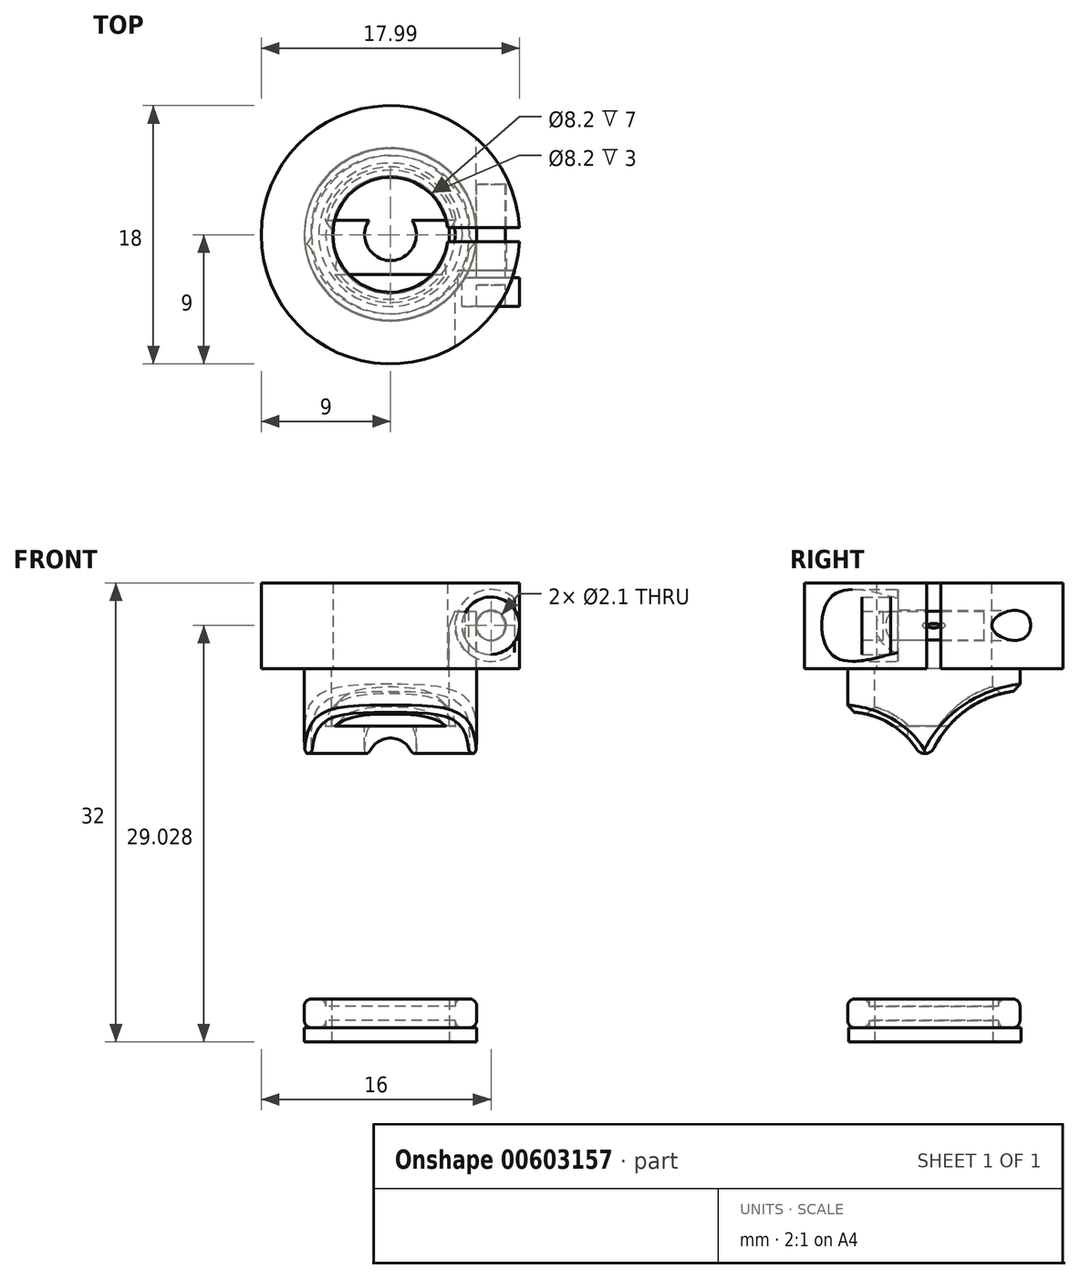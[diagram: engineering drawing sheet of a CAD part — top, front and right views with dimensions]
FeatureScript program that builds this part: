
annotation { "Feature Type Name" : "Feature", "Feature Type Description" : "" }
export const myFeature = defineFeature(function(context is Context, id is Id, definition is map)
    precondition{}
    {
        {
            var Q0;
            Q0=qCreatedBy(makeId("Top.planeOp"),FACE);
            var sketch = newSketch(context, id + "F0", { "sketchPlane" : qUnion([Q0])});
            skCircle(sketch, "E0", {"center": v(0, 0) * mm, "radius": 6 * mm});
            skCircle(sketch, "E1", {"center": v(0, 0) * mm, "radius": 4.5 * mm});
            skSolve(sketch);
        }
        {
            var Q0;
            Q0=makeQuery(id+"F0.imprint","IMPRINT",FACE,{"disambiguationData":[TD([[makeQuery(id+"F0.imprint","IMPRINT",EDGE,{"derivedFrom":sQuery(id+"F0.wireOp",EDGE,"E0")}),1.0]])]});
            extrude(context, id + "F1", {"entities" : qUnion([Q0]), "depth" : 2 * mm, "offsetDistance" : 25 * mm});
        }
        {
            var Q0;
            Q0=makeQuery(id+"F1.opExtrude","CAP_EDGE",EDGE,{"disambiguationData":[OSD([sQuery(id+"F0.wireOp",EDGE,"E0")])],"isStart":false});
            var Q1;
            Q1=makeQuery(id+"F1.opExtrude","CAP_EDGE",EDGE,{"disambiguationData":[OSD([sQuery(id+"F0.wireOp",EDGE,"E1")])],"isStart":false});
            var Q2;
            Q2=makeQuery(id+"F1.opExtrude","CAP_EDGE",EDGE,{"disambiguationData":[OSD([sQuery(id+"F0.wireOp",EDGE,"E0")])],"isStart":true});
            var Q3;
            Q3=makeQuery(id+"F1.opExtrude","CAP_EDGE",EDGE,{"disambiguationData":[OSD([sQuery(id+"F0.wireOp",EDGE,"E1")])],"isStart":true});
            fillet(context, id + "F2", {"entities" : qUnion([Q0, Q1, Q2, Q3]), "radius" : .5 * mm, "tangentPropagation" : true, "allowEdgeOverflow" : false});
        }
        {
            var Q0;
            Q0=qCreatedBy(makeId("Top.planeOp"),FACE);
            var sketch = newSketch(context, id + "F3", { "sketchPlane" : qUnion([Q0])});
            skCircle(sketch, "E2", {"center": v(0, 0) * mm, "radius": 4.1 * mm});
            skCircle(sketch, "E3", {"center": v(0, 0.06) * mm, "radius": 6 * mm});
            skCircle(sketch, "E4", {"center": v(0, 0) * mm, "radius": 4.5 * mm});
            skSolve(sketch);
        }
        {
            var Q0;
            Q0=makeQuery(id+"F3.imprint","IMPRINT",FACE,{"disambiguationData":[TD([[makeQuery(id+"F3.imprint","IMPRINT",EDGE,{"derivedFrom":sQuery(id+"F3.wireOp",EDGE,"E2")}),-1.0]])]});
            extrude(context, id + "F4", {"entities" : qUnion([Q0]), "depth" : 2 * mm, "offsetDistance" : 25 * mm});
        }
        {
            var Q0;
            Q0=makeQuery(id+"F3.imprint","IMPRINT",FACE,{"disambiguationData":[TD([[makeQuery(id+"F3.imprint","IMPRINT",EDGE,{"derivedFrom":sQuery(id+"F3.wireOp",EDGE,"E2")}),-1.0]])]});
            var Q1;
            Q1=makeQuery(id+"F3.imprint","IMPRINT",FACE,{"disambiguationData":[TD([[makeQuery(id+"F3.imprint","IMPRINT",EDGE,{"derivedFrom":sQuery(id+"F3.wireOp",EDGE,"E3")}),1.0]])]});
            extrude(context, id + "F5", {"entities" : qUnion([Q0, Q1]), "operationType" : NewBodyOperationType.ADD, "oppositeDirection" : true, "depth" : 1 * mm, "offsetDistance" : 25 * mm});
        }
        {
            var Q0;
            Q0=qCreatedBy(makeId("Top.planeOp"),FACE);
            cPlane(context, id + "F6", {"entities" : qUnion([Q0]), "cplaneType" : CPlaneType.OFFSET, "offset" : 25 * mm, "width" : 150 * mm, "height" : 150 * mm});
        }
        {
            var Q0;
            Q0=qCreatedBy(id+"F6.planeOp",FACE);
            var sketch = newSketch(context, id + "F7", { "sketchPlane" : qUnion([Q0])});
            skCircle(sketch, "E5", {"center": v(0, 0) * mm, "radius": 4 * mm});
            skCircle(sketch, "E6", {"center": v(0, 0) * mm, "radius": 9 * mm});
            skLineSegment(sketch, "E7", {"start": v(3.97, 0.5) * mm, "end": v(8.99, 0.5) * mm});
            skLineSegment(sketch, "E8.MirrorCS", {"start": v(3.97, -0.5) * mm, "end": v(8.99, -0.5) * mm});
            skSolve(sketch);
        }
        {
            var Q0;
            {var subQ0=sQuery(id+"F7.wireOp",EDGE,"E7");Q0=makeQuery(id+"F7.imprint","IMPRINT",FACE,{"disambiguationData":[TD([[makeQuery(id+"F7.imprint","IMPRINT",EDGE,{"derivedFrom":subQ0}),1.0]])]});}
            extrude(context, id + "F8", {"entities" : qUnion([Q0]), "depth" : 6 * mm, "offsetDistance" : 25 * mm});
        }
        {
            var Q0;
            Q0=qCreatedBy(makeId("Front.planeOp"),FACE);
            var sketch = newSketch(context, id + "F9", { "sketchPlane" : qUnion([Q0])});
            skCircle(sketch, "E9", {"center": v(7, 28.03) * mm, "radius": 2.5 * mm});
            skSolve(sketch);
        }
        {
            var Q0;
            Q0=sQuery(id+"F9.wireOp",VERTEX,"E9.center");
            var Q1;
            Q1=makeQuery(id+"F8.opExtrude","SWEPT_BODY",BODY,{"disambiguationData":[OSD([sQuery(id+"F7.wireOp",EDGE,"E5"),sQuery(id+"F7.wireOp",EDGE,"E6"),sQuery(id+"F7.wireOp",EDGE,"E7"),sQuery(id+"F7.wireOp",EDGE,"E8.MirrorCS")])]});
            hole(context, id + "F10", {"style" : HoleStyle.SIMPLE, "endStyle" : HoleEndStyle.THROUGH, "holeDiameter" : 2.1 * mm, "majorDiameter" : 5 * mm, "isTappedThrough" : true, "tappedDepth" : 6 * mm, "tapClearance" : 3, "startFromSketch" : true, "locations" : qUnion([Q0]), "scope" : qUnion([Q1])});
        }
        {
            var Q0;
            Q0=sQuery(id+"F9.wireOp",VERTEX,"E9.center");
            var Q1;
            Q1=makeQuery(id+"F8.opExtrude","SWEPT_BODY",BODY,{"disambiguationData":[OSD([sQuery(id+"F7.wireOp",EDGE,"E5"),sQuery(id+"F7.wireOp",EDGE,"E6"),sQuery(id+"F7.wireOp",EDGE,"E7"),sQuery(id+"F7.wireOp",EDGE,"E8.MirrorCS")])]});
            hole(context, id + "F11", {"style" : HoleStyle.SIMPLE, "endStyle" : HoleEndStyle.THROUGH, "oppositeDirection" : true, "holeDiameter" : 2.1 * mm, "majorDiameter" : 5 * mm, "isTappedThrough" : true, "tappedDepth" : 6 * mm, "tapClearance" : 3, "startFromSketch" : true, "locations" : qUnion([Q0]), "scope" : qUnion([Q1])});
        }
        {
            var Q0;
            Q0=makeQuery(id+"F9.imprint","IMPRINT",FACE,{"disambiguationData":[TD([[makeQuery(id+"F9.imprint","IMPRINT",EDGE,{"derivedFrom":sQuery(id+"F9.wireOp",EDGE,"E9")}),1.0]])]});
            var Q1;
            Q1=sQuery(id+"F9.wireOp",EDGE,"E9");
            extrude(context, id + "F12", {"entities" : qUnion([Q0]), "operationType" : NewBodyOperationType.REMOVE, "surfaceEntities" : qUnion([Q1]), "depth" : 10 * mm, "offsetDistance" : 25 * mm, "hasSecondDirection" : true, "secondDirectionOppositeDirection" : false, "secondDirectionDepth" : 2.5 * mm});
        }
        {
            var Q0;
            Q0=qCreatedBy(makeId("Front.planeOp"),FACE);
            var sketch = newSketch(context, id + "F13", { "sketchPlane" : qUnion([Q0])});
            skCircle(sketch, "E10", {"center": v(6.99, 28) * mm, "radius": 2 * mm});
            skCircle(sketch, "E11", {"center": v(6.99, 28) * mm, "radius": 1 * mm});
            skSolve(sketch);
        }
        {
            var Q0;
            Q0=makeQuery(id+"F13.imprint","IMPRINT",FACE,{"disambiguationData":[TD([[makeQuery(id+"F13.imprint","IMPRINT",EDGE,{"derivedFrom":sQuery(id+"F13.wireOp",EDGE,"E11")}),1.0]])]});
            extrude(context, id + "F14", {"entities" : qUnion([Q0]), "depth" : 7 * mm, "offsetDistance" : 25 * mm, "symmetric" : true});
        }
        {
            var Q0;
            Q0=makeQuery(id+"F13.imprint","IMPRINT",FACE,{"disambiguationData":[TD([[makeQuery(id+"F13.imprint","IMPRINT",EDGE,{"derivedFrom":sQuery(id+"F13.wireOp",EDGE,"E10")}),1.0]])]});
            extrude(context, id + "F15", {"entities" : qUnion([Q0]), "operationType" : NewBodyOperationType.ADD, "depth" : 5 * mm, "offsetDistance" : 25 * mm, "hasSecondDirection" : true, "secondDirectionOppositeDirection" : false, "secondDirectionDepth" : 3 * mm});
        }
        {
            var Q0;
            Q0=makeQuery(id+"F8.opExtrude","CAP_FACE",FACE,{"disambiguationData":[OSD([sQuery(id+"F7.wireOp",EDGE,"E5"),sQuery(id+"F7.wireOp",EDGE,"E6"),sQuery(id+"F7.wireOp",EDGE,"E7"),sQuery(id+"F7.wireOp",EDGE,"E8.MirrorCS")])],"isStart":true});
            var sketch = newSketch(context, id + "F16", { "sketchPlane" : qUnion([Q0])});
            skCircle(sketch, "E12", {"center": v(0, 0) * mm, "radius": 4.1 * mm});
            skCircle(sketch, "E13", {"center": v(0, 0) * mm, "radius": 6 * mm});
            skSolve(sketch);
        }
        {
            var Q0;
            {var subQ0=sQuery(id+"F16.wireOp",EDGE,"E12");var subQ1=makeQuery(id+"F8.opExtrude","CAP_EDGE",EDGE,{"disambiguationData":[OSD([sQuery(id+"F7.wireOp",EDGE,"E7")])],"isStart":true});var subQ2=makeQuery(id+"F16.imprint","INTERSECT",VERTEX,{"derivedFrom":[subQ1,subQ0]});Q0=makeQuery(id+"F16.imprint","IMPRINT",FACE,{"disambiguationData":[TD([[makeQuery(id+"F16.imprint","IMPRINT",EDGE,{"disambiguationData":[TD([[subQ2,1.0]])],"derivedFrom":subQ0}),-1.0]])]});}
            var Q1;
            {var subQ0=sQuery(id+"F16.wireOp",EDGE,"E12");var subQ1=makeQuery(id+"F8.opExtrude","CAP_EDGE",EDGE,{"disambiguationData":[OSD([sQuery(id+"F7.wireOp",EDGE,"E7")])],"isStart":true});var subQ2=makeQuery(id+"F16.imprint","INTERSECT",VERTEX,{"derivedFrom":[subQ1,subQ0]});Q1=makeQuery(id+"F16.imprint","IMPRINT",FACE,{"disambiguationData":[TD([[makeQuery(id+"F16.imprint","IMPRINT",EDGE,{"disambiguationData":[TD([[subQ2,-1.0]])],"derivedFrom":subQ0}),-1.0]])]});}
            extrude(context, id + "F17", {"entities" : qUnion([Q0, Q1]), "depth" : 4 * mm, "offsetDistance" : 25 * mm});
        }
        {
            var Q0;
            Q0=makeQuery(id+"F17.opExtrude","CAP_FACE",FACE,{"disambiguationData":[OSD([sQuery(id+"F16.wireOp",EDGE,"E12"),sQuery(id+"F16.wireOp",EDGE,"E13")])],"isStart":false});
            var sketch = newSketch(context, id + "F18", { "sketchPlane" : qUnion([Q0])});
            skCircle(sketch, "E14", {"center": v(0, 0) * mm, "radius": 1.8 * mm});
            skCircle(sketch, "E15", {"center": v(0, 0) * mm, "radius": 6 * mm});
            skSolve(sketch);
        }
        {
            var Q0;
            Q0 = qSketchRegion(id + "F18", true);
            extrude(context, id + "F19", {"entities" : qUnion([Q0]), "operationType" : NewBodyOperationType.ADD, "depth" : 3 * mm, "offsetDistance" : 25 * mm});
        }
        {
            var Q0;
            Q0=qCreatedBy(makeId("Right.planeOp"),FACE);
            var sketch = newSketch(context, id + "F20", { "sketchPlane" : qUnion([Q0])});
            skCircle(sketch, "E16", {"center": v(6.5, 16.25) * mm, "radius": 7.25 * mm});
            skCircle(sketch, "E17", {"center": v(-6, 16.25) * mm, "radius": 5.75 * mm});
            skSolve(sketch);
        }
        {
            var Q0;
            Q0=makeQuery(id+"F20.imprint","IMPRINT",FACE,{"disambiguationData":[TD([[makeQuery(id+"F20.imprint","IMPRINT",EDGE,{"derivedFrom":sQuery(id+"F20.wireOp",EDGE,"E16")}),1.0]])]});
            var Q1;
            Q1=makeQuery(id+"F20.imprint","IMPRINT",FACE,{"disambiguationData":[TD([[makeQuery(id+"F20.imprint","IMPRINT",EDGE,{"derivedFrom":sQuery(id+"F20.wireOp",EDGE,"E17")}),1.0]])]});
            extrude(context, id + "F21", {"entities" : qUnion([Q0, Q1]), "operationType" : NewBodyOperationType.REMOVE, "oppositeDirection" : true, "depth" : 25 * mm, "offsetDistance" : 25 * mm});
        }
        {
            var Q0;
            Q0=makeQuery(id+"F20.imprint","IMPRINT",FACE,{"disambiguationData":[TD([[makeQuery(id+"F20.imprint","IMPRINT",EDGE,{"derivedFrom":sQuery(id+"F20.wireOp",EDGE,"E16")}),1.0]])]});
            var Q1;
            Q1=makeQuery(id+"F20.imprint","IMPRINT",FACE,{"disambiguationData":[TD([[makeQuery(id+"F20.imprint","IMPRINT",EDGE,{"derivedFrom":sQuery(id+"F20.wireOp",EDGE,"E17")}),1.0]])]});
            extrude(context, id + "F22", {"entities" : qUnion([Q0, Q1]), "operationType" : NewBodyOperationType.REMOVE, "depth" : 25 * mm, "offsetDistance" : 25 * mm});
        }
        {
            var Q0;
            Q0=makeQuery(id+"F17.opExtrude","CAP_FACE",FACE,{"disambiguationData":[OSD([sQuery(id+"F16.wireOp",EDGE,"E12"),sQuery(id+"F16.wireOp",EDGE,"E13")])],"isStart":true});
            extrude(context, id + "F23", {"entities" : qUnion([Q0]), "operationType" : NewBodyOperationType.ADD, "depth" : 4 * mm, "offsetDistance" : 25 * mm});
        }
        {
            var Q0;
            Q0=makeQuery(id+"F22.boolean.opBoolean","INTERSECT",EDGE,{"derivedFrom":[makeQuery(id+"F17.opExtrude","SWEPT_FACE",FACE,{"disambiguationData":[OSD([sQuery(id+"F16.wireOp",EDGE,"E12")])]}),makeQuery(id+"F22.opExtrude","SWEPT_FACE",FACE,{"disambiguationData":[OSD([sQuery(id+"F20.wireOp",EDGE,"E16")])]})]});
            var Q1;
            Q1=makeQuery(id+"F22.boolean.opBoolean","INTERSECT",EDGE,{"derivedFrom":[makeQuery(id+"F17.opExtrude","SWEPT_FACE",FACE,{"disambiguationData":[OSD([sQuery(id+"F16.wireOp",EDGE,"E12")])]}),makeQuery(id+"F22.opExtrude","SWEPT_FACE",FACE,{"disambiguationData":[OSD([sQuery(id+"F20.wireOp",EDGE,"E17")])]})]});
            var Q2;
            Q2=makeQuery(id+"F22.boolean.opBoolean","INTERSECT",EDGE,{"derivedFrom":[makeQuery(id+"F19.boolean.opBoolean","MERGE",FACE,{"derivedFrom":[makeQuery(id+"F17.opExtrude","SWEPT_FACE",FACE,{"disambiguationData":[OSD([sQuery(id+"F16.wireOp",EDGE,"E13")])]}),makeQuery(id+"F19.opExtrude","SWEPT_FACE",FACE,{"disambiguationData":[OSD([sQuery(id+"F18.wireOp",EDGE,"E15")])]})]}),makeQuery(id+"F22.opExtrude","SWEPT_FACE",FACE,{"disambiguationData":[OSD([sQuery(id+"F20.wireOp",EDGE,"E16")])]})]});
            var Q3;
            Q3=makeQuery(id+"F22.boolean.opBoolean","INTERSECT",EDGE,{"derivedFrom":[makeQuery(id+"F19.boolean.opBoolean","MERGE",FACE,{"derivedFrom":[makeQuery(id+"F17.opExtrude","SWEPT_FACE",FACE,{"disambiguationData":[OSD([sQuery(id+"F16.wireOp",EDGE,"E13")])]}),makeQuery(id+"F19.opExtrude","SWEPT_FACE",FACE,{"disambiguationData":[OSD([sQuery(id+"F18.wireOp",EDGE,"E15")])]})]}),makeQuery(id+"F22.opExtrude","SWEPT_FACE",FACE,{"disambiguationData":[OSD([sQuery(id+"F20.wireOp",EDGE,"E17")])]})]});
            chamfer(context, id + "F24", {"entities" : qUnion([Q0, Q1, Q2, Q3]), "width" : .5 * mm, "tangentPropagation" : true});
        }
        {
            var Q0;
            Q0=makeQuery(id+"F23.opExtrude","CAP_EDGE",EDGE,{"disambiguationData":[OSD([sQuery(id+"F16.wireOp",EDGE,"E12")])],"isStart":false});
            chamfer(context, id + "F25", {"entities" : qUnion([Q0]), "chamferType" : ChamferType.TWO_OFFSETS, "width1" : .4 * mm, "oppositeDirection" : false, "width2" : 1 * mm, "tangentPropagation" : true});
        }
        {
            var Q0;
            {var subQ0=sQuery(id+"F20.wireOp",EDGE,"E17");var subQ1=sQuery(id+"F20.wireOp",EDGE,"E16");Q0=makeQuery(id+"F21.boolean.opBoolean","COPY",EDGE,{"derivedFrom":makeQuery(id+"F21.opExtrude","SWEPT_EDGE",EDGE,{"disambiguationData":[OSD([subQ1,subQ0]),TDD([makeQuery(id+"F20.imprint","INTERSECT",VERTEX,{"disambiguationData":[OD(1.0)],"derivedFrom":[subQ1,subQ0]})])]})});}
            var Q1;
            {var subQ0=sQuery(id+"F20.wireOp",EDGE,"E17");var subQ1=sQuery(id+"F20.wireOp",EDGE,"E16");Q1=makeQuery(id+"F22.boolean.opBoolean","COPY",EDGE,{"derivedFrom":makeQuery(id+"F22.opExtrude","SWEPT_EDGE",EDGE,{"disambiguationData":[OSD([subQ1,subQ0]),TDD([makeQuery(id+"F20.imprint","INTERSECT",VERTEX,{"disambiguationData":[OD(1.0)],"derivedFrom":[subQ1,subQ0]})])]})});}
            fillet(context, id + "F26", {"entities" : qUnion([Q0, Q1]), "radius" : .7 * mm, "tangentPropagation" : true, "allowEdgeOverflow" : false});
        }
    });
